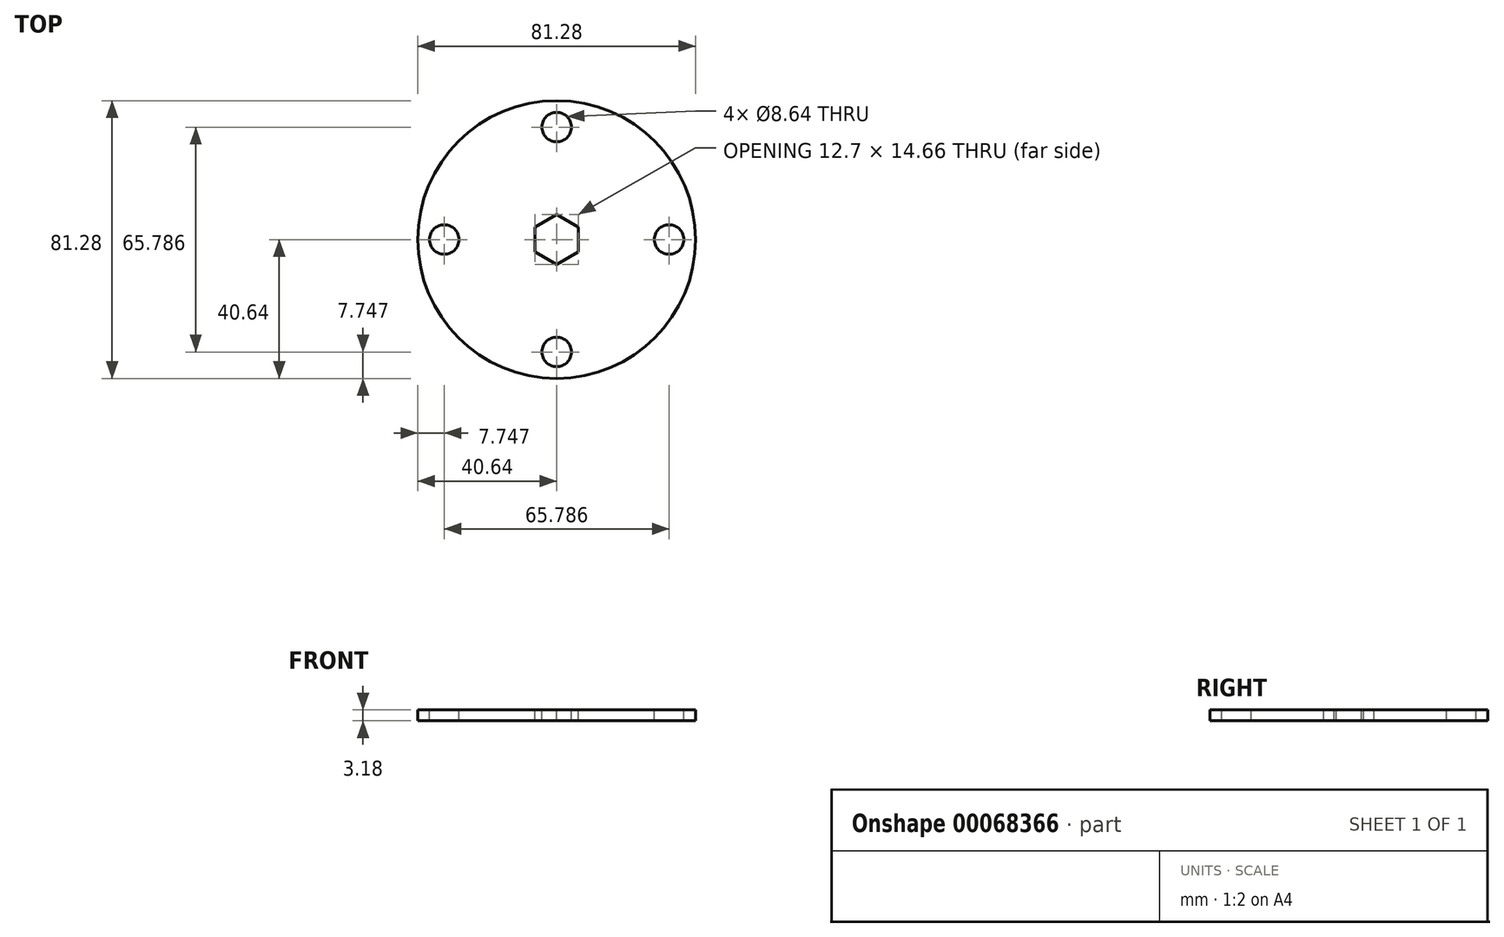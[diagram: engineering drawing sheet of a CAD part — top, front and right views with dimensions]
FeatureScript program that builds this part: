
annotation { "Feature Type Name" : "Feature", "Feature Type Description" : "" }
export const myFeature = defineFeature(function(context is Context, id is Id, definition is map)
    precondition{}
    {
        {
            var Q0;
            Q0=qCreatedBy(makeId("Top.planeOp"),FACE);
            var sketch = newSketch(context, id + "F0", { "sketchPlane" : qUnion([Q0])});
            skCircle(sketch, "E0", {"center": v(0, 0) * mm, "radius": 40.64 * mm});
            skSolve(sketch);
        }
        {
            var Q0;
            Q0 = qSketchRegion(id + "F0", true);
            extrude(context, id + "F1", {"entities" : qUnion([Q0]), "depth" : 3.17 * mm});
        }
        {
            var Q0;
            Q0=makeQuery(id+"F1.opExtrude","CAP_FACE",FACE,{"disambiguationData":[OSD([sQuery(id+"F0.wireOp",EDGE,"E0")])],"isStart":false});
            var sketch = newSketch(context, id + "F2", { "sketchPlane" : qUnion([Q0])});
            skCircle(sketch, "E1", {"center": v(-32.9, 0) * mm, "radius": 4.32 * mm});
            skCircle(sketch, "E2", {"center": v(0, -32.9) * mm, "radius": 4.32 * mm});
            skCircle(sketch, "E3", {"center": v(32.9, 0) * mm, "radius": 4.32 * mm});
            skCircle(sketch, "E4", {"center": v(0, 32.9) * mm, "radius": 4.32 * mm});
            skSolve(sketch);
        }
        {
            var Q0;
            Q0=makeQuery(id+"F2.imprint","IMPRINT",FACE,{"disambiguationData":[TD([[makeQuery(id+"F2.imprint","IMPRINT",EDGE,{"derivedFrom":sQuery(id+"F2.wireOp",EDGE,"E1")}),-1.0]])]});
            var sketch = newSketch(context, id + "F3", { "sketchPlane" : qUnion([Q0])});
            skCircle(sketch, "E5.cCircle", {"center": v(0, 0) * mm, "radius": 6.35 * mm, "construction": true});
            skLineSegment(sketch, "E5.0", {"start": v(6.35, 3.67) * mm, "end": v(6.35, -3.67) * mm});
            skLineSegment(sketch, "E5.1", {"start": v(6.35, -3.67) * mm, "end": v(0, -7.33) * mm});
            skLineSegment(sketch, "E5.2", {"start": v(0, -7.33) * mm, "end": v(-6.35, -3.67) * mm});
            skLineSegment(sketch, "E5.3", {"start": v(-6.35, -3.67) * mm, "end": v(-6.35, 3.67) * mm});
            skLineSegment(sketch, "E5.4", {"start": v(-6.35, 3.67) * mm, "end": v(0, 7.33) * mm});
            skLineSegment(sketch, "E5.5", {"start": v(0, 7.33) * mm, "end": v(6.35, 3.67) * mm});
            skPoint(sketch, "E5.0.midPoint", {"position": v(6.35, 0) * mm});
            skSolve(sketch);
        }
        {
            var Q0;
            Q0 = qSketchRegion(id + "F2", true);
            extrude(context, id + "F4", {"entities" : qUnion([Q0]), "operationType" : NewBodyOperationType.REMOVE, "oppositeDirection" : true, "depth" : 25.4 * mm});
        }
        {
            var Q0;
            Q0 = qSketchRegion(id + "F3", true);
            extrude(context, id + "F5", {"entities" : qUnion([Q0]), "operationType" : NewBodyOperationType.REMOVE, "oppositeDirection" : true, "depth" : 25.4 * mm});
        }
    });
